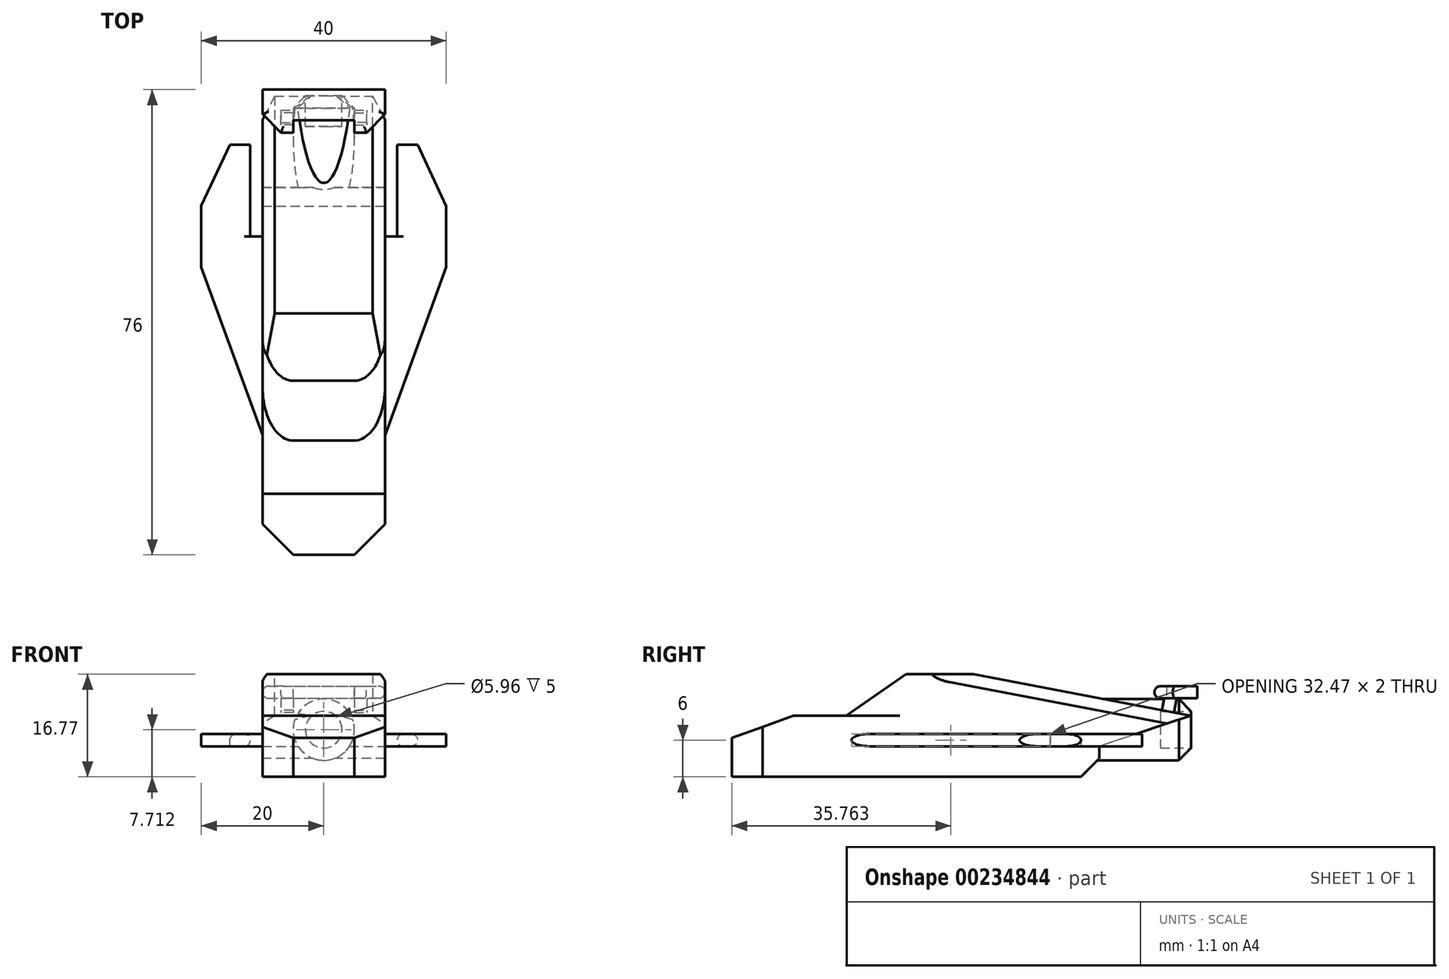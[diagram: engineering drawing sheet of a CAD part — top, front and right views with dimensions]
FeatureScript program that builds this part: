
annotation { "Feature Type Name" : "Feature", "Feature Type Description" : "" }
export const myFeature = defineFeature(function(context is Context, id is Id, definition is map)
    precondition{}
    {
        {
            var Q0;
            Q0=qCreatedBy(makeId("Right.planeOp"),FACE);
            var sketch = newSketch(context, id + "F0", { "sketchPlane" : qUnion([Q0])});
            skLineSegment(sketch, "E0", {"start": v(0, 0) * mm, "end": v(30, 0) * mm});
            skLineSegment(sketch, "E1", {"start": v(0, 0) * mm, "end": v(-30, 0) * mm});
            skLineSegment(sketch, "E2", {"start": v(30, 0) * mm, "end": v(30, -5) * mm});
            skLineSegment(sketch, "E3", {"start": v(30, -5) * mm, "end": v(-30, -5) * mm});
            skLineSegment(sketch, "E4", {"start": v(-30, -5) * mm, "end": v(-30, 0) * mm});
            skLineSegment(sketch, "E5", {"start": v(30, 0) * mm, "end": v(30, 5) * mm});
            skLineSegment(sketch, "E6", {"start": v(30, 5) * mm, "end": v(-30, 5) * mm});
            skLineSegment(sketch, "E7", {"start": v(-30, 5) * mm, "end": v(-30, 0) * mm});
            skLineSegment(sketch, "E8", {"start": v(-11.31, 5) * mm, "end": v(-1.57, 11.77) * mm});
            skLineSegment(sketch, "E9", {"start": v(-1.57, 11.77) * mm, "end": v(9.46, 11.77) * mm});
            skLineSegment(sketch, "E10", {"start": v(9.46, 11.77) * mm, "end": v(44.93, 5) * mm});
            skLineSegment(sketch, "E11", {"start": v(44.93, 5) * mm, "end": v(30, 0) * mm});
            skSolve(sketch);
        }
        {
            var Q0;
            {var subQ2=sQuery(id+"F0.wireOp",EDGE,"E5");Q0=makeQuery(id+"F0.imprint","IMPRINT",FACE,{"disambiguationData":[TD([[makeQuery(id+"F0.imprint","IMPRINT",EDGE,{"derivedFrom":subQ2}),-1.0]])]});}
            var Q1;
            Q1=makeQuery(id+"F0.imprint","IMPRINT",FACE,{"disambiguationData":[TD([[makeQuery(id+"F0.imprint","IMPRINT",EDGE,{"derivedFrom":sQuery(id+"F0.wireOp",EDGE,"E0")}),-1.0]])]});
            var Q2;
            Q2=makeQuery(id+"F0.imprint","IMPRINT",FACE,{"disambiguationData":[TD([[makeQuery(id+"F0.imprint","IMPRINT",EDGE,{"derivedFrom":sQuery(id+"F0.wireOp",EDGE,"E0")}),1.0]])]});
            extrude(context, id + "F1", {"entities" : qUnion([Q0, Q1, Q2]), "oppositeDirection" : true, "depth" : 10 * mm});
        }
        {
            var Q0;
            Q0=makeQuery(id+"F1.opExtrude","CAP_FACE",FACE,{"disambiguationData":[OSD([sQuery(id+"F0.wireOp",EDGE,"E2"),sQuery(id+"F0.wireOp",EDGE,"E3"),sQuery(id+"F0.wireOp",EDGE,"E4"),sQuery(id+"F0.wireOp",EDGE,"E6"),sQuery(id+"F0.wireOp",EDGE,"E7"),sQuery(id+"F0.wireOp",EDGE,"E8"),sQuery(id+"F0.wireOp",EDGE,"E9"),sQuery(id+"F0.wireOp",EDGE,"E10"),sQuery(id+"F0.wireOp",EDGE,"E11")])],"isStart":true});
            extrude(context, id + "F2", {"entities" : qUnion([Q0]), "operationType" : NewBodyOperationType.ADD, "depth" : 10 * mm});
        }
        {
            var Q0;
            Q0=makeQuery(id+"F1.opExtrude","CAP_EDGE",EDGE,{"disambiguationData":[OSD([sQuery(id+"F0.wireOp",EDGE,"E8")])],"isStart":false});
            var Q1;
            Q1=makeQuery(id+"F2.opExtrude","CAP_EDGE",EDGE,{"disambiguationData":[OSD([sQuery(id+"F0.wireOp",EDGE,"E8")])],"isStart":false});
            fillet(context, id + "F3", {"entities" : qUnion([Q0, Q1]), "radius" : 5 * mm, "tangentPropagation" : true, "allowEdgeOverflow" : false});
        }
        {
            var Q0;
            {var subQ0=sQuery(id+"F0.wireOp",EDGE,"E7");var subQ1=sQuery(id+"F0.wireOp",EDGE,"E6");Q0=makeQuery(id+"F2.boolean.opBoolean","MERGE",EDGE,{"derivedFrom":[makeQuery(id+"F1.opExtrude","SWEPT_EDGE",EDGE,{"disambiguationData":[OSD([subQ1,subQ0])]}),makeQuery(id+"F2.opExtrude","SWEPT_EDGE",EDGE,{"disambiguationData":[OSD([subQ1,subQ0])]})]});}
            chamfer(context, id + "F4", {"entities" : qUnion([Q0]), "chamferType" : ChamferType.OFFSET_ANGLE, "width" : 10 * mm, "oppositeDirection" : false, "angle" : 20 * degree, "tangentPropagation" : true});
        }
        {
            var Q0;
            Q0=makeQuery(id+"F1.opExtrude","CAP_EDGE",EDGE,{"disambiguationData":[OSD([sQuery(id+"F0.wireOp",EDGE,"E10")])],"isStart":false});
            var Q1;
            Q1=makeQuery(id+"F2.opExtrude","CAP_EDGE",EDGE,{"disambiguationData":[OSD([sQuery(id+"F0.wireOp",EDGE,"E10")])],"isStart":false});
            chamfer(context, id + "F5", {"entities" : qUnion([Q0, Q1]), "width" : 2 * mm, "tangentPropagation" : true});
        }
        {
            var Q0;
            {var subQ0=sQuery(id+"F0.wireOp",EDGE,"E3");var subQ1=sQuery(id+"F0.wireOp",EDGE,"E2");Q0=makeQuery(id+"F2.boolean.opBoolean","MERGE",EDGE,{"derivedFrom":[makeQuery(id+"F1.opExtrude","SWEPT_EDGE",EDGE,{"disambiguationData":[OSD([subQ1,subQ0])]}),makeQuery(id+"F2.opExtrude","SWEPT_EDGE",EDGE,{"disambiguationData":[OSD([subQ1,subQ0])]})]});}
            chamfer(context, id + "F6", {"entities" : qUnion([Q0]), "width" : 3 * mm, "tangentPropagation" : true});
        }
        {
            var Q0;
            Q0=makeQuery(id+"F1.opExtrude","CAP_EDGE",EDGE,{"disambiguationData":[OSD([sQuery(id+"F0.wireOp",EDGE,"E4"),sQuery(id+"F0.wireOp",EDGE,"E7")])],"isStart":false});
            var Q1;
            Q1=makeQuery(id+"F2.opExtrude","CAP_EDGE",EDGE,{"disambiguationData":[OSD([sQuery(id+"F0.wireOp",EDGE,"E4"),sQuery(id+"F0.wireOp",EDGE,"E7")])],"isStart":false});
            chamfer(context, id + "F7", {"entities" : qUnion([Q0, Q1]), "width" : 5 * mm, "tangentPropagation" : true});
        }
        {
            var Q0;
            Q0=makeQuery(id+"F2.opExtrude","CAP_FACE",FACE,{"disambiguationData":[OSD([sQuery(id+"F0.wireOp",EDGE,"E2"),sQuery(id+"F0.wireOp",EDGE,"E3"),sQuery(id+"F0.wireOp",EDGE,"E4"),sQuery(id+"F0.wireOp",EDGE,"E6"),sQuery(id+"F0.wireOp",EDGE,"E7"),sQuery(id+"F0.wireOp",EDGE,"E8"),sQuery(id+"F0.wireOp",EDGE,"E9"),sQuery(id+"F0.wireOp",EDGE,"E10"),sQuery(id+"F0.wireOp",EDGE,"E11")])],"isStart":false});
            var sketch = newSketch(context, id + "F8", { "sketchPlane" : qUnion([Q0])});
            skLineSegment(sketch, "E12", {"start": v(0, 0) * mm, "end": v(-13, 0) * mm});
            skLineSegment(sketch, "E13.bottom", {"start": v(-13, 0) * mm, "end": v(22, 0) * mm});
            skLineSegment(sketch, "E13.top", {"start": v(-13, 2) * mm, "end": v(22, 2) * mm});
            skLineSegment(sketch, "E13.left", {"start": v(-13, 0) * mm, "end": v(-13, 2) * mm});
            skLineSegment(sketch, "E13.right", {"start": v(22, 0) * mm, "end": v(22, 2) * mm});
            skSolve(sketch);
        }
        {
            var Q0;
            Q0=makeQuery(id+"F1.opExtrude","CAP_FACE",FACE,{"disambiguationData":[OSD([sQuery(id+"F0.wireOp",EDGE,"E2"),sQuery(id+"F0.wireOp",EDGE,"E3"),sQuery(id+"F0.wireOp",EDGE,"E4"),sQuery(id+"F0.wireOp",EDGE,"E6"),sQuery(id+"F0.wireOp",EDGE,"E7"),sQuery(id+"F0.wireOp",EDGE,"E8"),sQuery(id+"F0.wireOp",EDGE,"E9"),sQuery(id+"F0.wireOp",EDGE,"E10"),sQuery(id+"F0.wireOp",EDGE,"E11")])],"isStart":false});
            var sketch = newSketch(context, id + "F9", { "sketchPlane" : qUnion([Q0])});
            skLineSegment(sketch, "E14.bottom", {"start": v(12.97, 0) * mm, "end": v(-22.03, 0) * mm});
            skLineSegment(sketch, "E14.top", {"start": v(12.97, 2) * mm, "end": v(-22.03, 2) * mm});
            skLineSegment(sketch, "E14.left", {"start": v(12.97, 0) * mm, "end": v(12.97, 2) * mm});
            skLineSegment(sketch, "E14.right", {"start": v(-22.03, 0) * mm, "end": v(-22.03, 2) * mm});
            skSolve(sketch);
        }
        {
            var Q0;
            Q0=makeQuery(id+"F8.imprint","IMPRINT",FACE,{"disambiguationData":[TD([[makeQuery(id+"F8.imprint","IMPRINT",EDGE,{"derivedFrom":sQuery(id+"F8.wireOp",EDGE,"E13.top")}),-1.0]])]});
            extrude(context, id + "F10", {"entities" : qUnion([Q0]), "operationType" : NewBodyOperationType.ADD, "depth" : 10 * mm});
        }
        {
            var Q0;
            Q0=makeQuery(id+"F9.imprint","IMPRINT",FACE,{"disambiguationData":[TD([[makeQuery(id+"F9.imprint","IMPRINT",EDGE,{"derivedFrom":sQuery(id+"F9.wireOp",EDGE,"E14.bottom")}),-1.0]])]});
            extrude(context, id + "F11", {"entities" : qUnion([Q0]), "operationType" : NewBodyOperationType.ADD, "depth" : 10 * mm});
        }
        {
            var Q0;
            Q0=makeQuery(id+"F11.opExtrude","CAP_EDGE",EDGE,{"disambiguationData":[OSD([sQuery(id+"F9.wireOp",EDGE,"E14.left")])],"isStart":false});
            chamfer(context, id + "F12", {"entities" : qUnion([Q0]), "chamferType" : ChamferType.OFFSET_ANGLE, "width" : 30 * mm, "oppositeDirection" : false, "angle" : 20 * degree, "tangentPropagation" : true});
        }
        {
            var Q0;
            Q0=makeQuery(id+"F10.opExtrude","CAP_EDGE",EDGE,{"disambiguationData":[OSD([sQuery(id+"F8.wireOp",EDGE,"E13.left")])],"isStart":false});
            chamfer(context, id + "F13", {"entities" : qUnion([Q0]), "chamferType" : ChamferType.OFFSET_ANGLE, "width" : 30 * mm, "oppositeDirection" : true, "angle" : 20 * degree, "tangentPropagation" : true});
        }
        {
            var Q0;
            Q0=makeQuery(id+"F10.opExtrude","SWEPT_FACE",FACE,{"disambiguationData":[OSD([sQuery(id+"F8.wireOp",EDGE,"E13.right")])]});
            var sketch = newSketch(context, id + "F14", { "sketchPlane" : qUnion([Q0])});
            skLineSegment(sketch, "E15", {"start": v(-20, 0) * mm, "end": v(-12, 0) * mm});
            skLineSegment(sketch, "E16", {"start": v(-12, 0) * mm, "end": v(-12, 2) * mm});
            skLineSegment(sketch, "E17", {"start": v(-12, 2) * mm, "end": v(-20, 2) * mm});
            skLineSegment(sketch, "E18", {"start": v(-20, 2) * mm, "end": v(-20, 0) * mm});
            skSolve(sketch);
        }
        {
            var Q0;
            Q0=makeQuery(id+"F11.opExtrude","SWEPT_FACE",FACE,{"disambiguationData":[OSD([sQuery(id+"F9.wireOp",EDGE,"E14.right")])]});
            var sketch = newSketch(context, id + "F15", { "sketchPlane" : qUnion([Q0])});
            skLineSegment(sketch, "E19.bottom", {"start": v(20, 0) * mm, "end": v(12, 0) * mm});
            skLineSegment(sketch, "E19.top", {"start": v(20, 2) * mm, "end": v(12, 2) * mm});
            skLineSegment(sketch, "E19.left", {"start": v(20, 0) * mm, "end": v(20, 2) * mm});
            skLineSegment(sketch, "E19.right", {"start": v(12, 0) * mm, "end": v(12, 2) * mm});
            skSolve(sketch);
        }
        {
            var Q0;
            Q0=makeQuery(id+"F14.imprint","IMPRINT",FACE,{"disambiguationData":[TD([[makeQuery(id+"F14.imprint","IMPRINT",EDGE,{"derivedFrom":sQuery(id+"F14.wireOp",EDGE,"E15")}),1.0]])]});
            var Q1;
            Q1=makeQuery(id+"F15.imprint","IMPRINT",FACE,{"disambiguationData":[TD([[makeQuery(id+"F15.imprint","IMPRINT",EDGE,{"derivedFrom":sQuery(id+"F15.wireOp",EDGE,"E19.bottom")}),-1.0]])]});
            extrude(context, id + "F16", {"entities" : qUnion([Q0, Q1]), "operationType" : NewBodyOperationType.ADD, "depth" : 15 * mm});
        }
        {
            var Q0;
            Q0=makeQuery(id+"F16.opExtrude","CAP_EDGE",EDGE,{"disambiguationData":[OSD([sQuery(id+"F14.wireOp",EDGE,"E18")])],"isStart":false});
            chamfer(context, id + "F17", {"entities" : qUnion([Q0]), "chamferType" : ChamferType.OFFSET_ANGLE, "width" : 10 * mm, "oppositeDirection" : false, "angle" : 25 * degree, "tangentPropagation" : true});
        }
        {
            var Q0;
            Q0=makeQuery(id+"F16.opExtrude","CAP_EDGE",EDGE,{"disambiguationData":[OSD([sQuery(id+"F15.wireOp",EDGE,"E19.left")])],"isStart":false});
            chamfer(context, id + "F18", {"entities" : qUnion([Q0]), "chamferType" : ChamferType.OFFSET_ANGLE, "width" : 10 * mm, "oppositeDirection" : true, "angle" : 25 * degree, "tangentPropagation" : true});
        }
        {
            var Q0;
            Q0=makeQuery(id+"F13.opChamfer","BLEND_EDGE",EDGE,{"blendedFrom":[makeQuery(id+"F10.opExtrude","CAP_EDGE",EDGE,{"disambiguationData":[OSD([sQuery(id+"F8.wireOp",EDGE,"E13.left")])],"isStart":false}),makeQuery(id+"F10.opExtrude","SWEPT_FACE",FACE,{"disambiguationData":[OSD([sQuery(id+"F8.wireOp",EDGE,"E13.top")])]})],"blendedInto":[makeQuery(id+"F10.opExtrude","SWEPT_FACE",FACE,{"disambiguationData":[OSD([sQuery(id+"F8.wireOp",EDGE,"E13.top")])]})]});
            var Q1;
            Q1=makeQuery(id+"F13.opChamfer","BLEND_EDGE",EDGE,{"blendedFrom":[makeQuery(id+"F10.opExtrude","CAP_EDGE",EDGE,{"disambiguationData":[OSD([sQuery(id+"F8.wireOp",EDGE,"E13.left")])],"isStart":false}),makeQuery(id+"F10.opExtrude","SWEPT_FACE",FACE,{"disambiguationData":[OSD([sQuery(id+"F8.wireOp",EDGE,"E13.bottom")])]})],"blendedInto":[makeQuery(id+"F10.opExtrude","SWEPT_FACE",FACE,{"disambiguationData":[OSD([sQuery(id+"F8.wireOp",EDGE,"E13.bottom")])]})]});
            var Q2;
            Q2=makeQuery(id+"F17.opChamfer","BLEND_EDGE",EDGE,{"blendedFrom":[makeQuery(id+"F16.opExtrude","CAP_EDGE",EDGE,{"disambiguationData":[OSD([sQuery(id+"F14.wireOp",EDGE,"E18")])],"isStart":false}),makeQuery(id+"F16.boolean.opBoolean","MERGE",FACE,{"derivedFrom":[makeQuery(id+"F10.opExtrude","SWEPT_FACE",FACE,{"disambiguationData":[OSD([sQuery(id+"F8.wireOp",EDGE,"E13.bottom")])]}),makeQuery(id+"F16.opExtrude","SWEPT_FACE",FACE,{"disambiguationData":[OSD([sQuery(id+"F14.wireOp",EDGE,"E15")])]})]})],"blendedInto":[makeQuery(id+"F16.boolean.opBoolean","MERGE",FACE,{"derivedFrom":[makeQuery(id+"F10.opExtrude","SWEPT_FACE",FACE,{"disambiguationData":[OSD([sQuery(id+"F8.wireOp",EDGE,"E13.bottom")])]}),makeQuery(id+"F16.opExtrude","SWEPT_FACE",FACE,{"disambiguationData":[OSD([sQuery(id+"F14.wireOp",EDGE,"E15")])]})]})]});
            var Q3;
            Q3=makeQuery(id+"F17.opChamfer","BLEND_EDGE",EDGE,{"blendedFrom":[makeQuery(id+"F16.opExtrude","CAP_EDGE",EDGE,{"disambiguationData":[OSD([sQuery(id+"F14.wireOp",EDGE,"E18")])],"isStart":false}),makeQuery(id+"F16.boolean.opBoolean","MERGE",FACE,{"derivedFrom":[makeQuery(id+"F10.opExtrude","SWEPT_FACE",FACE,{"disambiguationData":[OSD([sQuery(id+"F8.wireOp",EDGE,"E13.top")])]}),makeQuery(id+"F16.opExtrude","SWEPT_FACE",FACE,{"disambiguationData":[OSD([sQuery(id+"F14.wireOp",EDGE,"E17")])]})]})],"blendedInto":[makeQuery(id+"F16.boolean.opBoolean","MERGE",FACE,{"derivedFrom":[makeQuery(id+"F10.opExtrude","SWEPT_FACE",FACE,{"disambiguationData":[OSD([sQuery(id+"F8.wireOp",EDGE,"E13.top")])]}),makeQuery(id+"F16.opExtrude","SWEPT_FACE",FACE,{"disambiguationData":[OSD([sQuery(id+"F14.wireOp",EDGE,"E17")])]})]})]});
            var Q4;
            Q4=makeQuery(id+"F16.opExtrude","SWEPT_EDGE",EDGE,{"disambiguationData":[OSD([sQuery(id+"F8.wireOp",EDGE,"E13.top"),sQuery(id+"F8.wireOp",EDGE,"E13.right"),sQuery(id+"F14.wireOp",EDGE,"E16"),sQuery(id+"F14.wireOp",EDGE,"E17")])]});
            var Q5;
            Q5=makeQuery(id+"F16.opExtrude","SWEPT_EDGE",EDGE,{"disambiguationData":[OSD([sQuery(id+"F8.wireOp",EDGE,"E13.bottom"),sQuery(id+"F8.wireOp",EDGE,"E13.right"),sQuery(id+"F14.wireOp",EDGE,"E15"),sQuery(id+"F14.wireOp",EDGE,"E16")])]});
            var Q6;
            Q6=makeQuery(id+"F12.opChamfer","BLEND_EDGE",EDGE,{"blendedFrom":[makeQuery(id+"F11.opExtrude","CAP_EDGE",EDGE,{"disambiguationData":[OSD([sQuery(id+"F9.wireOp",EDGE,"E14.left")])],"isStart":false}),makeQuery(id+"F11.opExtrude","SWEPT_FACE",FACE,{"disambiguationData":[OSD([sQuery(id+"F9.wireOp",EDGE,"E14.top")])]})],"blendedInto":[makeQuery(id+"F11.opExtrude","SWEPT_FACE",FACE,{"disambiguationData":[OSD([sQuery(id+"F9.wireOp",EDGE,"E14.top")])]})]});
            var Q7;
            Q7=makeQuery(id+"F12.opChamfer","BLEND_EDGE",EDGE,{"blendedFrom":[makeQuery(id+"F11.opExtrude","CAP_EDGE",EDGE,{"disambiguationData":[OSD([sQuery(id+"F9.wireOp",EDGE,"E14.left")])],"isStart":false}),makeQuery(id+"F11.opExtrude","SWEPT_FACE",FACE,{"disambiguationData":[OSD([sQuery(id+"F9.wireOp",EDGE,"E14.bottom")])]})],"blendedInto":[makeQuery(id+"F11.opExtrude","SWEPT_FACE",FACE,{"disambiguationData":[OSD([sQuery(id+"F9.wireOp",EDGE,"E14.bottom")])]})]});
            var Q8;
            Q8=makeQuery(id+"F18.opChamfer","BLEND_EDGE",EDGE,{"blendedFrom":[makeQuery(id+"F16.opExtrude","CAP_EDGE",EDGE,{"disambiguationData":[OSD([sQuery(id+"F15.wireOp",EDGE,"E19.left")])],"isStart":false}),makeQuery(id+"F16.boolean.opBoolean","MERGE",FACE,{"derivedFrom":[makeQuery(id+"F11.opExtrude","SWEPT_FACE",FACE,{"disambiguationData":[OSD([sQuery(id+"F9.wireOp",EDGE,"E14.top")])]}),makeQuery(id+"F16.opExtrude","SWEPT_FACE",FACE,{"disambiguationData":[OSD([sQuery(id+"F15.wireOp",EDGE,"E19.top")])]})]})],"blendedInto":[makeQuery(id+"F16.boolean.opBoolean","MERGE",FACE,{"derivedFrom":[makeQuery(id+"F11.opExtrude","SWEPT_FACE",FACE,{"disambiguationData":[OSD([sQuery(id+"F9.wireOp",EDGE,"E14.top")])]}),makeQuery(id+"F16.opExtrude","SWEPT_FACE",FACE,{"disambiguationData":[OSD([sQuery(id+"F15.wireOp",EDGE,"E19.top")])]})]})]});
            var Q9;
            Q9=makeQuery(id+"F16.opExtrude","SWEPT_EDGE",EDGE,{"disambiguationData":[OSD([sQuery(id+"F9.wireOp",EDGE,"E14.top"),sQuery(id+"F9.wireOp",EDGE,"E14.right"),sQuery(id+"F15.wireOp",EDGE,"E19.top"),sQuery(id+"F15.wireOp",EDGE,"E19.right")])]});
            var Q10;
            Q10=makeQuery(id+"F16.opExtrude","SWEPT_EDGE",EDGE,{"disambiguationData":[OSD([sQuery(id+"F9.wireOp",EDGE,"E14.bottom"),sQuery(id+"F9.wireOp",EDGE,"E14.right"),sQuery(id+"F15.wireOp",EDGE,"E19.bottom"),sQuery(id+"F15.wireOp",EDGE,"E19.right")])]});
            fillet(context, id + "F19", {"entities" : qUnion([Q0, Q1, Q2, Q3, Q4, Q5, Q6, Q7, Q8, Q9, Q10]), "radius" : 1 * mm, "tangentPropagation" : true, "allowEdgeOverflow" : false});
        }
        {
            var Q0;
            Q0=qCreatedBy(makeId("Front.planeOp"),FACE);
            var sketch = newSketch(context, id + "F20", { "sketchPlane" : qUnion([Q0])});
            skCircle(sketch, "E20", {"center": v(0, 2.71) * mm, "radius": 5 * mm});
            skSolve(sketch);
        }
        {
            var Q0;
            Q0=makeQuery(id+"F20.imprint","IMPRINT",FACE,{"disambiguationData":[TD([[makeQuery(id+"F20.imprint","IMPRINT",EDGE,{"derivedFrom":sQuery(id+"F20.wireOp",EDGE,"E20")}),1.0]])]});
            extrude(context, id + "F21", {"entities" : qUnion([Q0]), "operationType" : NewBodyOperationType.ADD, "oppositeDirection" : true, "depth" : 45 * mm});
        }
        {
            var Q0;
            Q0=makeQuery(id+"F21.opExtrude","CAP_FACE",FACE,{"disambiguationData":[OSD([sQuery(id+"F20.wireOp",EDGE,"E20")])],"isStart":false});
            var sketch = newSketch(context, id + "F22", { "sketchPlane" : qUnion([Q0])});
            skCircle(sketch, "E21", {"center": v(0, 2.71) * mm, "radius": 2.98 * mm});
            skSolve(sketch);
        }
        {
            var Q0;
            Q0=makeQuery(id+"F22.imprint","IMPRINT",FACE,{"disambiguationData":[TD([[makeQuery(id+"F22.imprint","IMPRINT",EDGE,{"derivedFrom":sQuery(id+"F22.wireOp",EDGE,"E21")}),1.0]])]});
            extrude(context, id + "F23", {"entities" : qUnion([Q0]), "operationType" : NewBodyOperationType.REMOVE, "oppositeDirection" : true, "depth" : 5 * mm});
        }
        {
            var Q0;
            Q0=makeQuery(id+"F21.opExtrude","CAP_EDGE",EDGE,{"disambiguationData":[OSD([sQuery(id+"F20.wireOp",EDGE,"E20")])],"isStart":false});
            chamfer(context, id + "F24", {"entities" : qUnion([Q0]), "width" : 2 * mm, "tangentPropagation" : true});
        }
        {
            var Q0;
            {var subQ0=sQuery(id+"F0.wireOp",EDGE,"E10");Q0=makeQuery(id+"F2.boolean.opBoolean","MERGE",FACE,{"derivedFrom":[makeQuery(id+"F1.opExtrude","SWEPT_FACE",FACE,{"disambiguationData":[OSD([subQ0])]}),makeQuery(id+"F2.opExtrude","SWEPT_FACE",FACE,{"disambiguationData":[OSD([subQ0])]})]});}
            var sketch = newSketch(context, id + "F25", { "sketchPlane" : qUnion([Q0])});
            skLineSegment(sketch, "E22", {"start": v(0, 38.42) * mm, "end": v(-5, 38.42) * mm});
            skLineSegment(sketch, "E23", {"start": v(-5, 38.42) * mm, "end": v(5, 38.42) * mm});
            skLineSegment(sketch, "E24.bottom", {"start": v(-5, 38.42) * mm, "end": v(-7, 38.42) * mm});
            skLineSegment(sketch, "E24.top", {"start": v(-5, 40.42) * mm, "end": v(-7, 40.42) * mm});
            skLineSegment(sketch, "E24.left", {"start": v(-5, 38.42) * mm, "end": v(-5, 40.42) * mm});
            skLineSegment(sketch, "E24.right", {"start": v(-7, 38.42) * mm, "end": v(-7, 40.42) * mm});
            skLineSegment(sketch, "E25.bottom", {"start": v(5, 38.42) * mm, "end": v(7, 38.42) * mm});
            skLineSegment(sketch, "E25.top", {"start": v(5, 40.42) * mm, "end": v(7, 40.42) * mm});
            skLineSegment(sketch, "E25.left", {"start": v(5, 38.42) * mm, "end": v(5, 40.42) * mm});
            skLineSegment(sketch, "E25.right", {"start": v(7, 38.42) * mm, "end": v(7, 40.42) * mm});
            skSolve(sketch);
        }
        {
            var Q0;
            Q0=makeQuery(id+"F25.imprint","IMPRINT",FACE,{"disambiguationData":[TD([[makeQuery(id+"F25.imprint","IMPRINT",EDGE,{"derivedFrom":sQuery(id+"F25.wireOp",EDGE,"E24.bottom")}),-1.0]])]});
            var Q1;
            Q1=makeQuery(id+"F25.imprint","IMPRINT",FACE,{"disambiguationData":[TD([[makeQuery(id+"F25.imprint","IMPRINT",EDGE,{"derivedFrom":sQuery(id+"F25.wireOp",EDGE,"E25.bottom")}),1.0]])]});
            extrude(context, id + "F26", {"entities" : qUnion([Q0, Q1]), "operationType" : NewBodyOperationType.ADD, "depth" : 4 * mm});
        }
        {
            var Q0;
            Q0=makeQuery(id+"F26.opExtrude","SWEPT_FACE",FACE,{"disambiguationData":[OSD([sQuery(id+"F25.wireOp",EDGE,"E25.left")])]});
            var sketch = newSketch(context, id + "F27", { "sketchPlane" : qUnion([Q0])});
            skLineSegment(sketch, "E26.bottom", {"start": v(-41, 9.82) * mm, "end": v(-46, 9.82) * mm});
            skLineSegment(sketch, "E26.top", {"start": v(-41, 7.82) * mm, "end": v(-46, 7.82) * mm});
            skLineSegment(sketch, "E26.left", {"start": v(-41, 9.82) * mm, "end": v(-41, 7.82) * mm});
            skLineSegment(sketch, "E26.right", {"start": v(-46, 9.82) * mm, "end": v(-46, 7.82) * mm});
            skSolve(sketch);
        }
        {
            var Q0;
            Q0=makeQuery(id+"F27.imprint","IMPRINT",FACE,{"disambiguationData":[TD([[makeQuery(id+"F27.imprint","IMPRINT",EDGE,{"derivedFrom":sQuery(id+"F27.wireOp",EDGE,"E26.bottom")}),1.0]])]});
            var Q1;
            {var subQ0=sQuery(id+"F27.wireOp",EDGE,"E26.left");Q1=makeQuery(id+"F27.imprint","IMPRINT",FACE,{"disambiguationData":[TD([[makeQuery(id+"F27.imprint","IMPRINT",EDGE,{"derivedFrom":subQ0}),-1.0]])]});}
            extrude(context, id + "F28", {"entities" : qUnion([Q0, Q1]), "operationType" : NewBodyOperationType.ADD, "depth" : 15 * mm});
        }
        {
            var Q0;
            Q0=makeQuery(id+"F27.imprint","IMPRINT",FACE,{"disambiguationData":[TD([[makeQuery(id+"F27.imprint","IMPRINT",EDGE,{"derivedFrom":sQuery(id+"F27.wireOp",EDGE,"E26.bottom")}),1.0]])]});
            var Q1;
            {var subQ0=sQuery(id+"F27.wireOp",EDGE,"E26.left");Q1=makeQuery(id+"F27.imprint","IMPRINT",FACE,{"disambiguationData":[TD([[makeQuery(id+"F27.imprint","IMPRINT",EDGE,{"derivedFrom":subQ0}),-1.0]])]});}
            extrude(context, id + "F29", {"entities" : qUnion([Q0, Q1]), "operationType" : NewBodyOperationType.ADD, "oppositeDirection" : true, "depth" : 5 * mm});
        }
        {
            var Q0;
            {var subQ4=sQuery(id+"F27.wireOp",EDGE,"E26.left");Q0=makeQuery(id+"F28.boolean.opBoolean","SPLIT",FACE,{"disambiguationData":[TD([makeQuery(id+"F26.opExtrude","SWEPT_FACE",FACE,{"disambiguationData":[OSD([sQuery(id+"F25.wireOp",EDGE,"E24.left")])]})])],"derivedFrom":makeQuery(id+"F28.opExtrude","SWEPT_FACE",FACE,{"disambiguationData":[OSD([subQ4])]})});}
            var sketch = newSketch(context, id + "F30", { "sketchPlane" : qUnion([Q0])});
            skLineSegment(sketch, "E27", {"start": v(0, 7.82) * mm, "end": v(-10, 7.82) * mm});
            skLineSegment(sketch, "E28", {"start": v(-10, 7.82) * mm, "end": v(-10, 9.82) * mm});
            skLineSegment(sketch, "E29", {"start": v(-10, 9.82) * mm, "end": v(0, 9.82) * mm});
            skLineSegment(sketch, "E30", {"start": v(0, 9.82) * mm, "end": v(10, 9.82) * mm});
            skLineSegment(sketch, "E31", {"start": v(10, 9.82) * mm, "end": v(10, 7.82) * mm});
            skLineSegment(sketch, "E32", {"start": v(10, 7.82) * mm, "end": v(0, 7.82) * mm});
            skSolve(sketch);
        }
        {
            var Q0;
            {var subQ2=sQuery(id+"F30.wireOp",EDGE,"E28");Q0=makeQuery(id+"F30.imprint","IMPRINT",FACE,{"disambiguationData":[TD([[makeQuery(id+"F30.imprint","IMPRINT",EDGE,{"derivedFrom":subQ2}),-1.0]])]});}
            var Q1;
            {var subQ1=sQuery(id+"F27.wireOp",EDGE,"E26.left");var subQ2=makeQuery(id+"F28.opExtrude","CAP_EDGE",EDGE,{"disambiguationData":[OSD([subQ1])],"isStart":true});Q1=makeQuery(id+"F30.imprint","IMPRINT",FACE,{"disambiguationData":[TD([[makeQuery(id+"F30.imprint","IMPRINT",EDGE,{"derivedFrom":subQ2}),-1.0]])]});}
            var Q2;
            {var subQ2=sQuery(id+"F30.wireOp",EDGE,"E31");Q2=makeQuery(id+"F30.imprint","IMPRINT",FACE,{"disambiguationData":[TD([[makeQuery(id+"F30.imprint","IMPRINT",EDGE,{"derivedFrom":subQ2}),-1.0]])]});}
            extrude(context, id + "F31", {"entities" : qUnion([Q0, Q1, Q2]), "operationType" : NewBodyOperationType.ADD, "depth" : 2 * mm});
        }
        {
            var Q0;
            Q0=makeQuery(id+"F31.opExtrude","CAP_EDGE",EDGE,{"disambiguationData":[OSD([sQuery(id+"F30.wireOp",EDGE,"E28")])],"isStart":false});
            var Q1;
            Q1=makeQuery(id+"F31.opExtrude","CAP_EDGE",EDGE,{"disambiguationData":[OSD([sQuery(id+"F30.wireOp",EDGE,"E31")])],"isStart":false});
            chamfer(context, id + "F32", {"entities" : qUnion([Q0, Q1]), "width" : 3 * mm, "tangentPropagation" : true});
        }
        {
            var Q0;
            Q0=makeQuery(id+"F31.opExtrude","CAP_EDGE",EDGE,{"disambiguationData":[OSD([sQuery(id+"F30.wireOp",EDGE,"E27"),sQuery(id+"F30.wireOp",EDGE,"E32")])],"isStart":false});
            var Q1;
            Q1=makeQuery(id+"F31.opExtrude","CAP_EDGE",EDGE,{"disambiguationData":[OSD([sQuery(id+"F30.wireOp",EDGE,"E29"),sQuery(id+"F30.wireOp",EDGE,"E30")])],"isStart":false});
            var Q2;
            {var subQ0=sQuery(id+"F27.wireOp",EDGE,"E26.bottom");Q2=makeQuery(id+"F32.opChamfer","BLEND_EDGE",EDGE,{"blendedFrom":[makeQuery(id+"F31.opExtrude","CAP_EDGE",EDGE,{"disambiguationData":[OSD([sQuery(id+"F30.wireOp",EDGE,"E28")])],"isStart":false}),makeQuery(id+"F31.boolean.opBoolean","MERGE",FACE,{"derivedFrom":[makeQuery(id+"F29.boolean.opBoolean","MERGE",FACE,{"derivedFrom":[makeQuery(id+"F28.opExtrude","SWEPT_FACE",FACE,{"disambiguationData":[OSD([subQ0])]}),makeQuery(id+"F29.opExtrude","SWEPT_FACE",FACE,{"disambiguationData":[OSD([subQ0])]})]}),makeQuery(id+"F31.opExtrude","SWEPT_FACE",FACE,{"disambiguationData":[OSD([sQuery(id+"F30.wireOp",EDGE,"E29"),sQuery(id+"F30.wireOp",EDGE,"E30")])]})]})],"blendedInto":[makeQuery(id+"F31.boolean.opBoolean","MERGE",FACE,{"derivedFrom":[makeQuery(id+"F29.boolean.opBoolean","MERGE",FACE,{"derivedFrom":[makeQuery(id+"F28.opExtrude","SWEPT_FACE",FACE,{"disambiguationData":[OSD([subQ0])]}),makeQuery(id+"F29.opExtrude","SWEPT_FACE",FACE,{"disambiguationData":[OSD([subQ0])]})]}),makeQuery(id+"F31.opExtrude","SWEPT_FACE",FACE,{"disambiguationData":[OSD([sQuery(id+"F30.wireOp",EDGE,"E29"),sQuery(id+"F30.wireOp",EDGE,"E30")])]})]})]});}
            var Q3;
            {var subQ0=sQuery(id+"F27.wireOp",EDGE,"E26.top");Q3=makeQuery(id+"F32.opChamfer","BLEND_EDGE",EDGE,{"blendedFrom":[makeQuery(id+"F31.opExtrude","CAP_EDGE",EDGE,{"disambiguationData":[OSD([sQuery(id+"F30.wireOp",EDGE,"E28")])],"isStart":false}),makeQuery(id+"F31.boolean.opBoolean","MERGE",FACE,{"derivedFrom":[makeQuery(id+"F29.boolean.opBoolean","MERGE",FACE,{"derivedFrom":[makeQuery(id+"F28.opExtrude","SWEPT_FACE",FACE,{"disambiguationData":[OSD([subQ0])]}),makeQuery(id+"F29.opExtrude","SWEPT_FACE",FACE,{"disambiguationData":[OSD([subQ0])]})]}),makeQuery(id+"F31.opExtrude","SWEPT_FACE",FACE,{"disambiguationData":[OSD([sQuery(id+"F30.wireOp",EDGE,"E27"),sQuery(id+"F30.wireOp",EDGE,"E32")])]})]})],"blendedInto":[makeQuery(id+"F31.boolean.opBoolean","MERGE",FACE,{"derivedFrom":[makeQuery(id+"F29.boolean.opBoolean","MERGE",FACE,{"derivedFrom":[makeQuery(id+"F28.opExtrude","SWEPT_FACE",FACE,{"disambiguationData":[OSD([subQ0])]}),makeQuery(id+"F29.opExtrude","SWEPT_FACE",FACE,{"disambiguationData":[OSD([subQ0])]})]}),makeQuery(id+"F31.opExtrude","SWEPT_FACE",FACE,{"disambiguationData":[OSD([sQuery(id+"F30.wireOp",EDGE,"E27"),sQuery(id+"F30.wireOp",EDGE,"E32")])]})]})]});}
            var Q4;
            {var subQ0=sQuery(id+"F27.wireOp",EDGE,"E26.bottom");Q4=makeQuery(id+"F32.opChamfer","BLEND_EDGE",EDGE,{"blendedFrom":[makeQuery(id+"F31.opExtrude","CAP_EDGE",EDGE,{"disambiguationData":[OSD([sQuery(id+"F30.wireOp",EDGE,"E31")])],"isStart":false}),makeQuery(id+"F31.boolean.opBoolean","MERGE",FACE,{"derivedFrom":[makeQuery(id+"F29.boolean.opBoolean","MERGE",FACE,{"derivedFrom":[makeQuery(id+"F28.opExtrude","SWEPT_FACE",FACE,{"disambiguationData":[OSD([subQ0])]}),makeQuery(id+"F29.opExtrude","SWEPT_FACE",FACE,{"disambiguationData":[OSD([subQ0])]})]}),makeQuery(id+"F31.opExtrude","SWEPT_FACE",FACE,{"disambiguationData":[OSD([sQuery(id+"F30.wireOp",EDGE,"E29"),sQuery(id+"F30.wireOp",EDGE,"E30")])]})]})],"blendedInto":[makeQuery(id+"F31.boolean.opBoolean","MERGE",FACE,{"derivedFrom":[makeQuery(id+"F29.boolean.opBoolean","MERGE",FACE,{"derivedFrom":[makeQuery(id+"F28.opExtrude","SWEPT_FACE",FACE,{"disambiguationData":[OSD([subQ0])]}),makeQuery(id+"F29.opExtrude","SWEPT_FACE",FACE,{"disambiguationData":[OSD([subQ0])]})]}),makeQuery(id+"F31.opExtrude","SWEPT_FACE",FACE,{"disambiguationData":[OSD([sQuery(id+"F30.wireOp",EDGE,"E29"),sQuery(id+"F30.wireOp",EDGE,"E30")])]})]})]});}
            var Q5;
            {var subQ0=sQuery(id+"F27.wireOp",EDGE,"E26.top");Q5=makeQuery(id+"F32.opChamfer","BLEND_EDGE",EDGE,{"blendedFrom":[makeQuery(id+"F31.opExtrude","CAP_EDGE",EDGE,{"disambiguationData":[OSD([sQuery(id+"F30.wireOp",EDGE,"E31")])],"isStart":false}),makeQuery(id+"F31.boolean.opBoolean","MERGE",FACE,{"derivedFrom":[makeQuery(id+"F29.boolean.opBoolean","MERGE",FACE,{"derivedFrom":[makeQuery(id+"F28.opExtrude","SWEPT_FACE",FACE,{"disambiguationData":[OSD([subQ0])]}),makeQuery(id+"F29.opExtrude","SWEPT_FACE",FACE,{"disambiguationData":[OSD([subQ0])]})]}),makeQuery(id+"F31.opExtrude","SWEPT_FACE",FACE,{"disambiguationData":[OSD([sQuery(id+"F30.wireOp",EDGE,"E27"),sQuery(id+"F30.wireOp",EDGE,"E32")])]})]})],"blendedInto":[makeQuery(id+"F31.boolean.opBoolean","MERGE",FACE,{"derivedFrom":[makeQuery(id+"F29.boolean.opBoolean","MERGE",FACE,{"derivedFrom":[makeQuery(id+"F28.opExtrude","SWEPT_FACE",FACE,{"disambiguationData":[OSD([subQ0])]}),makeQuery(id+"F29.opExtrude","SWEPT_FACE",FACE,{"disambiguationData":[OSD([subQ0])]})]}),makeQuery(id+"F31.opExtrude","SWEPT_FACE",FACE,{"disambiguationData":[OSD([sQuery(id+"F30.wireOp",EDGE,"E27"),sQuery(id+"F30.wireOp",EDGE,"E32")])]})]})]});}
            var Q6;
            Q6=makeQuery(id+"F31.boolean.opBoolean","MERGE",EDGE,{"derivedFrom":[makeQuery(id+"F29.opExtrude","CAP_EDGE",EDGE,{"disambiguationData":[OSD([sQuery(id+"F27.wireOp",EDGE,"E26.top")])],"isStart":false}),makeQuery(id+"F31.opExtrude","SWEPT_EDGE",EDGE,{"disambiguationData":[OSD([sQuery(id+"F30.wireOp",EDGE,"E31"),sQuery(id+"F30.wireOp",EDGE,"E32")])]})]});
            var Q7;
            Q7=makeQuery(id+"F31.boolean.opBoolean","MERGE",EDGE,{"derivedFrom":[makeQuery(id+"F29.opExtrude","CAP_EDGE",EDGE,{"disambiguationData":[OSD([sQuery(id+"F27.wireOp",EDGE,"E26.bottom")])],"isStart":false}),makeQuery(id+"F31.opExtrude","SWEPT_EDGE",EDGE,{"disambiguationData":[OSD([sQuery(id+"F30.wireOp",EDGE,"E30"),sQuery(id+"F30.wireOp",EDGE,"E31")])]})]});
            var Q8;
            Q8=makeQuery(id+"F31.boolean.opBoolean","MERGE",EDGE,{"derivedFrom":[makeQuery(id+"F28.opExtrude","CAP_EDGE",EDGE,{"disambiguationData":[OSD([sQuery(id+"F27.wireOp",EDGE,"E26.bottom")])],"isStart":false}),makeQuery(id+"F31.opExtrude","SWEPT_EDGE",EDGE,{"disambiguationData":[OSD([sQuery(id+"F30.wireOp",EDGE,"E28"),sQuery(id+"F30.wireOp",EDGE,"E29")])]})]});
            var Q9;
            Q9=makeQuery(id+"F31.boolean.opBoolean","MERGE",EDGE,{"derivedFrom":[makeQuery(id+"F28.opExtrude","CAP_EDGE",EDGE,{"disambiguationData":[OSD([sQuery(id+"F27.wireOp",EDGE,"E26.top")])],"isStart":false}),makeQuery(id+"F31.opExtrude","SWEPT_EDGE",EDGE,{"disambiguationData":[OSD([sQuery(id+"F30.wireOp",EDGE,"E27"),sQuery(id+"F30.wireOp",EDGE,"E28")])]})]});
            fillet(context, id + "F33", {"entities" : qUnion([Q0, Q1, Q2, Q3, Q4, Q5, Q6, Q7, Q8, Q9]), "radius" : 1 * mm, "tangentPropagation" : true, "allowEdgeOverflow" : false});
        }
    });
